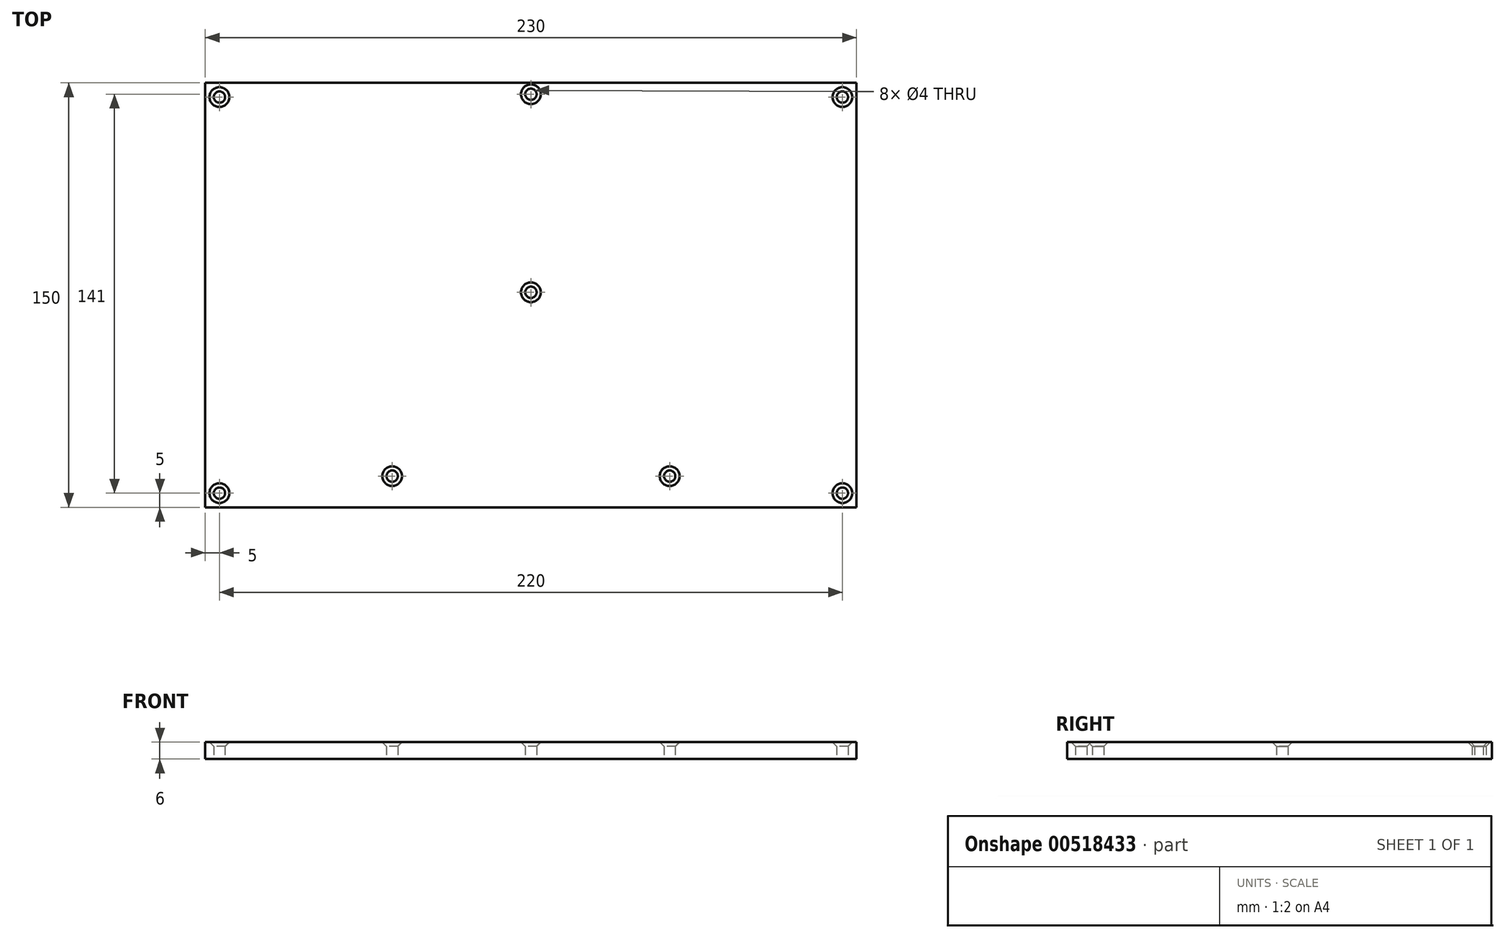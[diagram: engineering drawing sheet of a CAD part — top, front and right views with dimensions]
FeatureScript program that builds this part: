
annotation { "Feature Type Name" : "Feature", "Feature Type Description" : "" }
export const myFeature = defineFeature(function(context is Context, id is Id, definition is map)
    precondition{}
    {
        {
            var Q0;
            Q0=qCreatedBy(makeId("Top.planeOp"),FACE);
            var sketch = newSketch(context, id + "F0", { "sketchPlane" : qUnion([Q0])});
            skLineSegment(sketch, "E0.bottom", {"start": v(0, 0) * mm, "end": v(230, 0) * mm});
            skLineSegment(sketch, "E0.top", {"start": v(0, 150) * mm, "end": v(230, 150) * mm});
            skLineSegment(sketch, "E0.left", {"start": v(0, 0) * mm, "end": v(0, 150) * mm});
            skLineSegment(sketch, "E0.right", {"start": v(230, 0) * mm, "end": v(230, 150) * mm});
            skCircle(sketch, "E1", {"center": v(5, 145) * mm, "radius": 2 * mm});
            skCircle(sketch, "E2", {"center": v(5, 5) * mm, "radius": 2 * mm});
            skCircle(sketch, "E3", {"center": v(225, 5) * mm, "radius": 2 * mm});
            skCircle(sketch, "E4", {"center": v(225, 145) * mm, "radius": 2 * mm});
            skCircle(sketch, "E5", {"center": v(115, 146) * mm, "radius": 2 * mm});
            skCircle(sketch, "E6", {"center": v(115, 76) * mm, "radius": 2 * mm});
            skCircle(sketch, "E7", {"center": v(66, 11) * mm, "radius": 2 * mm});
            skCircle(sketch, "E8", {"center": v(164, 11) * mm, "radius": 2 * mm});
            skLineSegment(sketch, "E9", {"start": v(164, 11) * mm, "end": v(66, 11) * mm, "construction": true});
            skLineSegment(sketch, "E10", {"start": v(115, 11) * mm, "end": v(115, 76) * mm, "construction": true});
            skSolve(sketch);
        }
        {
            var Q0;
            Q0 = qSketchRegion(id + "F0", true);
            extrude(context, id + "F1", {"entities" : qUnion([Q0]), "depth" : 6 * mm, "offsetDistance" : 25 * mm});
        }
        {
            var Q0;
            Q0=makeQuery(id+"F1.opExtrude","CAP_EDGE",EDGE,{"disambiguationData":[OSD([sQuery(id+"F0.wireOp",EDGE,"E1")])],"isStart":false});
            var Q1;
            Q1=makeQuery(id+"F1.opExtrude","CAP_EDGE",EDGE,{"disambiguationData":[OSD([sQuery(id+"F0.wireOp",EDGE,"E2")])],"isStart":false});
            var Q2;
            Q2=makeQuery(id+"F1.opExtrude","CAP_EDGE",EDGE,{"disambiguationData":[OSD([sQuery(id+"F0.wireOp",EDGE,"E7")])],"isStart":false});
            var Q3;
            Q3=makeQuery(id+"F1.opExtrude","CAP_EDGE",EDGE,{"disambiguationData":[OSD([sQuery(id+"F0.wireOp",EDGE,"E6")])],"isStart":false});
            var Q4;
            Q4=makeQuery(id+"F1.opExtrude","CAP_EDGE",EDGE,{"disambiguationData":[OSD([sQuery(id+"F0.wireOp",EDGE,"E5")])],"isStart":false});
            var Q5;
            Q5=makeQuery(id+"F1.opExtrude","CAP_EDGE",EDGE,{"disambiguationData":[OSD([sQuery(id+"F0.wireOp",EDGE,"E8")])],"isStart":false});
            var Q6;
            Q6=makeQuery(id+"F1.opExtrude","CAP_EDGE",EDGE,{"disambiguationData":[OSD([sQuery(id+"F0.wireOp",EDGE,"E3")])],"isStart":false});
            var Q7;
            Q7=makeQuery(id+"F1.opExtrude","CAP_EDGE",EDGE,{"disambiguationData":[OSD([sQuery(id+"F0.wireOp",EDGE,"E4")])],"isStart":false});
            chamfer(context, id + "F2", {"entities" : qUnion([Q0, Q1, Q2, Q3, Q4, Q5, Q6, Q7]), "width" : 1.5 * mm, "tangentPropagation" : true});
        }
    });
